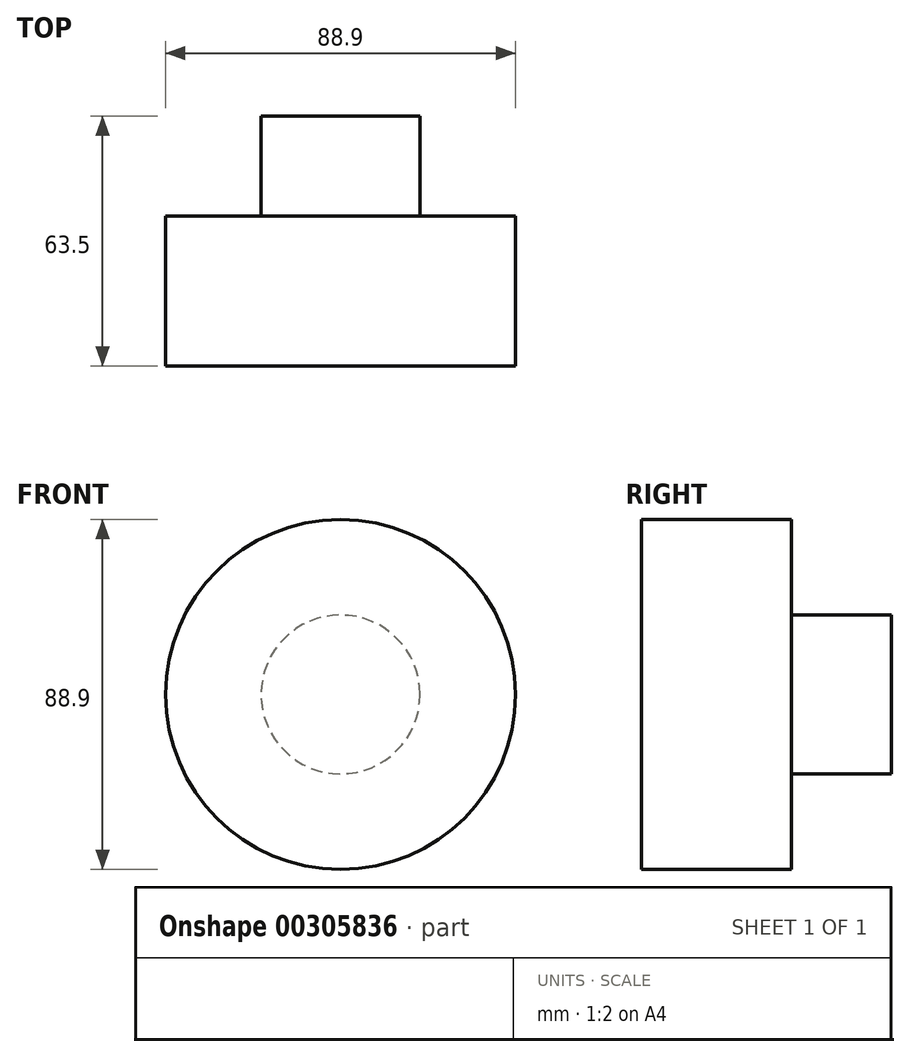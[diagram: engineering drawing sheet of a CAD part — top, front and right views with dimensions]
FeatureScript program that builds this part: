
annotation { "Feature Type Name" : "Feature", "Feature Type Description" : "" }
export const myFeature = defineFeature(function(context is Context, id is Id, definition is map)
    precondition{}
    {
        {
            var Q0;
            Q0=qCreatedBy(makeId("Front.planeOp"),FACE);
            var sketch = newSketch(context, id + "F0", { "sketchPlane" : qUnion([Q0])});
            skCircle(sketch, "E0", {"center": v(0, 0) * mm, "radius": 31.75 * mm});
            skCircle(sketch, "E1", {"center": v(0, 0) * mm, "radius": 44.45 * mm});
            skSolve(sketch);
        }
        {
            var Q0;
            Q0=makeQuery(id+"F0.imprint","IMPRINT",FACE,{"disambiguationData":[TD([[makeQuery(id+"F0.imprint","IMPRINT",EDGE,{"derivedFrom":sQuery(id+"F0.wireOp",EDGE,"E0")}),1.0]])]});
            var Q1;
            Q1=makeQuery(id+"F0.imprint","IMPRINT",FACE,{"disambiguationData":[TD([[makeQuery(id+"F0.imprint","IMPRINT",EDGE,{"derivedFrom":sQuery(id+"F0.wireOp",EDGE,"E0")}),-1.0]])]});
            extrude(context, id + "F1", {"entities" : qUnion([Q0, Q1]), "depth" : 38.1 * mm});
        }
        {
            var Q0;
            Q0=makeQuery(id+"F1.opExtrude","CAP_FACE",FACE,{"disambiguationData":[OSD([sQuery(id+"F0.wireOp",EDGE,"E1")])],"isStart":true});
            var sketch = newSketch(context, id + "F2", { "sketchPlane" : qUnion([Q0])});
            skCircle(sketch, "E2", {"center": v(0, 0) * mm, "radius": 20.18 * mm});
            skSolve(sketch);
        }
        {
            var Q0;
            Q0 = qSketchRegion(id + "F2", true);
            extrude(context, id + "F3", {"entities" : qUnion([Q0]), "operationType" : NewBodyOperationType.ADD, "depth" : 25.4 * mm});
        }
        {
            var Q0;
            Q0=makeQuery(id+"F1.opExtrude","CAP_FACE",FACE,{"disambiguationData":[OSD([sQuery(id+"F0.wireOp",EDGE,"E1")])],"isStart":false});
            var sketch = newSketch(context, id + "F4", { "sketchPlane" : qUnion([Q0])});
            skCircle(sketch, "E3", {"center": v(0, 0) * mm, "radius": 23.97 * mm});
            skSolve(sketch);
        }
        {
            var Q0;
            Q0 = qSketchRegion(id + "F4", true);
            extrude(context, id + "F5", {"entities" : qUnion([Q0]), "operationType" : NewBodyOperationType.ADD, "oppositeDirection" : true, "depth" : 25.65 * mm});
        }
        {
            var Q0;
            Q0=makeQuery(id+"F1.opExtrude","CAP_FACE",FACE,{"disambiguationData":[OSD([sQuery(id+"F0.wireOp",EDGE,"E1")])],"isStart":false});
            var sketch = newSketch(context, id + "F6", { "sketchPlane" : qUnion([Q0])});
            skCircle(sketch, "E4", {"center": v(0, 0) * mm, "radius": 12.85 * mm});
            skSolve(sketch);
        }
    });
